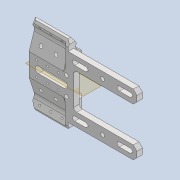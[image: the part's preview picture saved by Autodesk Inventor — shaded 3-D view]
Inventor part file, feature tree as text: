
AUTODESK INVENTOR PART (.ipt)
format: ipt  version: 2020 (Build 240168000, 168)  size: 702,976 bytes
history: native  units: mm
features: reference x19, projected_geometry x19, sketch x16, extrude x14, thicken_offset x13, fillet x7, other x7, mirror x4, chamfer x4, plane x3, hole x2
ambient origin geometry x8: Origin, YZ Plane, XZ Plane, XY Plane, X Axis, Y Axis, Z Axis, Center Point
bodies: Solid1 (feature_tree)
feature tree (108):
  sketch  "Sketch1"  dims[d0=5.0mm d1=7.0mm]
  plane  "Work Plane1"
  extrude  "Extrusion1"  Depth=7.0mm
  sketch  "Sketch2"  dims[d2=5.0mm d3=7.0mm]
  plane  "Work Plane2"
  extrude  "Extrusion2"  Depth=7.0mm
  hole  "Hole1"  [1 undecoded]
  plane  "Work Plane3"
  mirror  "Mirror1"
  extrude  "Extrusion3"  Depth=10.0mm
  thicken_offset  "Thicken1"
  thicken_offset  "Thicken2"
  thicken_offset  "Thicken3"
  extrude  "Extrusion4"  Depth=10.0mm
  extrude  "Extrusion5"  Depth=20.0mm TaperAngle=0.0deg
  thicken_offset  "Thicken4"
  thicken_offset  "Thicken5"
  extrude  "Extrusion6"  Depth=1.0mm
  extrude  "Extrusion7"  Depth=1.0mm
  fillet  "Fillet2"  Radius=1.0mm
  fillet  "Fillet3"  Radius=1.0mm
  fillet  "Fillet4"  Radius=2.9mm
  thicken_offset  "Thicken6"
  thicken_offset  "Thicken7"
  fillet  "Fillet5"  Radius=1.45mm
  chamfer  "Chamfer1"  Distance=21.5mm
  extrude  "Extrusion8"  Depth=1.0mm
  fillet  "Fillet6"  Radius=1.0mm
  chamfer  "Chamfer2"  Distance=20.0mm
  extrude  "Extrusion9"  Depth=0.5mm
  fillet  "Fillet7"  Radius=0.5mm
  mirror  "Mirror2"
  hole  "Hole2"  [1 undecoded]
  extrude  "Extrusion10"  Depth=10.0mm
  extrude  "Extrusion11"  Depth=10.0mm
  mirror  "Mirror3"
  extrude  "Extrusion12"  Depth=1.0mm
  mirror  "Mirror4"
  chamfer  "Chamfer3"  Distance=0.5mm
  fillet  "Fillet8"  Radius=0.5mm
  thicken_offset  "Thicken8"
  thicken_offset  "Thicken9"
  thicken_offset  "Thicken10"
  thicken_offset  "Thicken11"
  thicken_offset  "Thicken12"
  thicken_offset  "Thicken13"
  extrude  "Extrusion14"  Depth=10.0mm
  extrude  "Extrusion15"  Depth=10.0mm
  chamfer  "Chamfer4"  Distance=3.0mm
  reference  "Reference1"
  reference  "Reference2"
  reference  "Reference3"
  reference  "Reference4"
  reference  "Reference5"
  reference  "Reference6"
  reference  "Reference7"
  reference  "Reference8"
  reference  "Reference9"
  reference  "Reference10"
  reference  "Reference11"
  reference  "Reference12"
  reference  "Reference13"
  reference  "Reference14"
  projected_geometry  "Projected Loop1"
  sketch  "Sketch3"  dims[d4=3.0mm d5=21.0mm]
  reference  "Reference15"
  reference  "Reference16"
  reference  "Reference17"
  sketch  "Sketch4"  dims[d6=10.0mm d7=0.0mm d8=2.0mm]
  projected_geometry  "Projected Loop2"
  projected_geometry  "Projected Loop3"
  sketch  "Sketch5"  dims[d9=10.0mm d10=0.0mm]
  projected_geometry  "Projected Loop4"
  sketch  "Sketch6"  dims[d11=1.1mm d12=6.0mm d13=4.0mm d14=2.0mm d15=90.0deg d16=10.0mm d17=0.0mm d18=2.0mm]
  projected_geometry  "Projected Loop5"
  projected_geometry  "Projected Loop6"
  projected_geometry  "Projected Loop7"
  sketch  "Sketch7"  dims[d19=2.0mm d20=20.0mm d21=0.0mm]
  projected_geometry  "Projected Loop8"
  projected_geometry  "Projected Loop9"
  sketch  "Sketch8"  dims[d22=1.0mm d23=1.0mm]
  projected_geometry  "Projected Loop10"
  sketch  "Sketch9"  dims[d24=1.0mm d25=1.0mm d26=1.0mm d27=1.0mm d28=2.9mm d29=1.45mm]
  projected_geometry  "Projected Loop11"
  projected_geometry  "Projected Loop12"
  sketch  "Sketch10"  dims[d30=2.9mm]
  projected_geometry  "Projected Loop13"
  sketch  "Sketch11"  dims[d31=12.0mm d32=21.5mm d33=0.0mm]
  projected_geometry  "Projected Loop14"
  sketch  "Sketch12"  dims[d35=1.0mm d36=1.0mm d37=1.0mm]
  projected_geometry  "Projected Loop15"
  sketch  "Sketch13"  dims[d38=1.0mm d39=20.0mm d40=0.0mm]
  projected_geometry  "Projected Loop16"
  sketch  "Sketch14"  dims[d41=0.5mm d42=0.5mm d43=0.5mm]
  projected_geometry  "Projected Loop17"
  sketch  "Sketch15"  dims[d44=0.5mm d45=20.0mm d46=0.0mm]
  reference  "Reference18"
  reference  "Reference19"
  projected_geometry  "Projected Loop18"
  sketch  "Sketch16"  dims[d47=0.1mm d48=0.0mm d49=0.4mm d50=0.6mm d51=1.0mm d52=0.5mm d53=0.5mm d54=0.5mm d55=0.5mm d56=3.0mm d57=1.5mm d58=2.0mm d59=45.0deg d60=2.0mm d61=0.0mm d62=1.0mm d63=1.5mm d64=2.0mm d65=45.0deg d66=3.5mm d67=3.5mm d68=1.5mm d69=30.0mm d70=0.0mm d71=1.0mm d72=4.0mm d73=6.0mm d74=6.0mm d75=4.0mm d76=4.0mm d77=4.0mm d78=4.0mm d79=4.0mm d80=4.0mm d81=1.1mm d82=6.0mm d83=4.0mm d84=2.0mm d85=90.0deg d86=10.0mm d87=0.0mm d88=7.0mm d89=3.5mm d90=30.0mm d91=0.0mm d92=4.0mm d93=1.0mm d94=2.0mm d95=30.0mm d96=0.0mm d97=5.0mm d98=8.0mm d99=2.0mm d100=2.0mm d101=30.0mm d102=0.0mm d103=2.0mm d104=2.0mm d105=45.0deg d106=1.5mm d107=30.0mm d108=30.0mm d109=30.0mm d110=30.0mm d111=1.0mm d112=1.0mm d113=1.0mm d114=1.0mm d115=1.0mm d116=1.0mm d117=1.0mm d118=1.0mm d119=6.0mm d120=2.4mm d121=6.0mm d122=2.4mm d123=6.0mm d124=2.4mm d125=6.0mm d126=2.4mm d129=10.0mm d130=0.0mm d131=2.0mm d132=2.0mm d133=10.0mm d134=0.0mm d135=2.0mm d136=2.0mm d137=45.0deg]
  projected_geometry  "Projected Loop19"
  parser-record x2  (decoder bookkeeping rows leaked as tree rows — omitted from the tree; the rows remain in map.json)
  other  "tip_3_n_ass.iam"
  other  "end_shell_n_1:1"
  other  "bl_tube_ass_2:1"
  other  "bl_tube_hn_1:1"
  other  "tip_3_n_base_ass.iam"
note: 2 required parameter values undecoded (feature->parameter linkage not recoverable at this tier; creation-order binding heuristic only, values carry confidence <= 0.55)
note: 2 file-system paths scrubbed to <path> (originals preserved in map.json)
